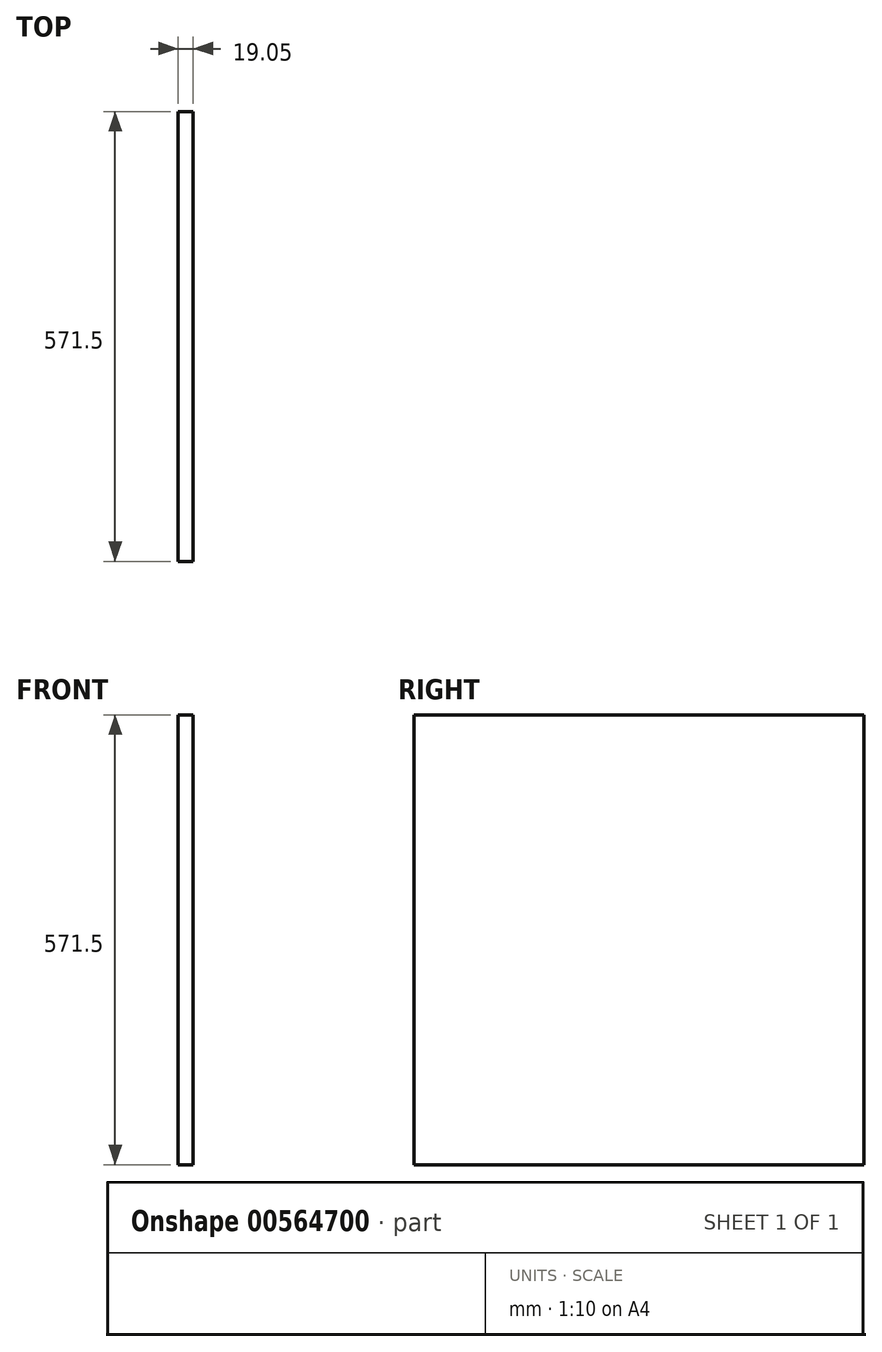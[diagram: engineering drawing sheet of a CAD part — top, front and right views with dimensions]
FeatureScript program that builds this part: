
annotation { "Feature Type Name" : "Feature", "Feature Type Description" : "" }
export const myFeature = defineFeature(function(context is Context, id is Id, definition is map)
    precondition{}
    {
        {
            var Q0;
            Q0=qCreatedBy(makeId("Right.planeOp"),FACE);
            var sketch = newSketch(context, id + "F0", { "sketchPlane" : qUnion([Q0])});
            skLineSegment(sketch, "E0.bottom", {"start": v(285.75, 285.75) * mm, "end": v(-285.75, 285.75) * mm});
            skLineSegment(sketch, "E0.top", {"start": v(285.75, -285.75) * mm, "end": v(-285.75, -285.75) * mm});
            skLineSegment(sketch, "E0.left", {"start": v(285.75, 285.75) * mm, "end": v(285.75, -285.75) * mm});
            skLineSegment(sketch, "E0.right", {"start": v(-285.75, 285.75) * mm, "end": v(-285.75, -285.75) * mm});
            skPoint(sketch, "E0.middle", {"position": v(0, 0) * mm});
            skSolve(sketch);
        }
        {
            var Q0;
            Q0 = qSketchRegion(id + "F0", true);
            extrude(context, id + "F1", {"entities" : qUnion([Q0]), "depth" : 19.05 * mm, "offsetDistance" : 25.4 * mm});
        }
    });
